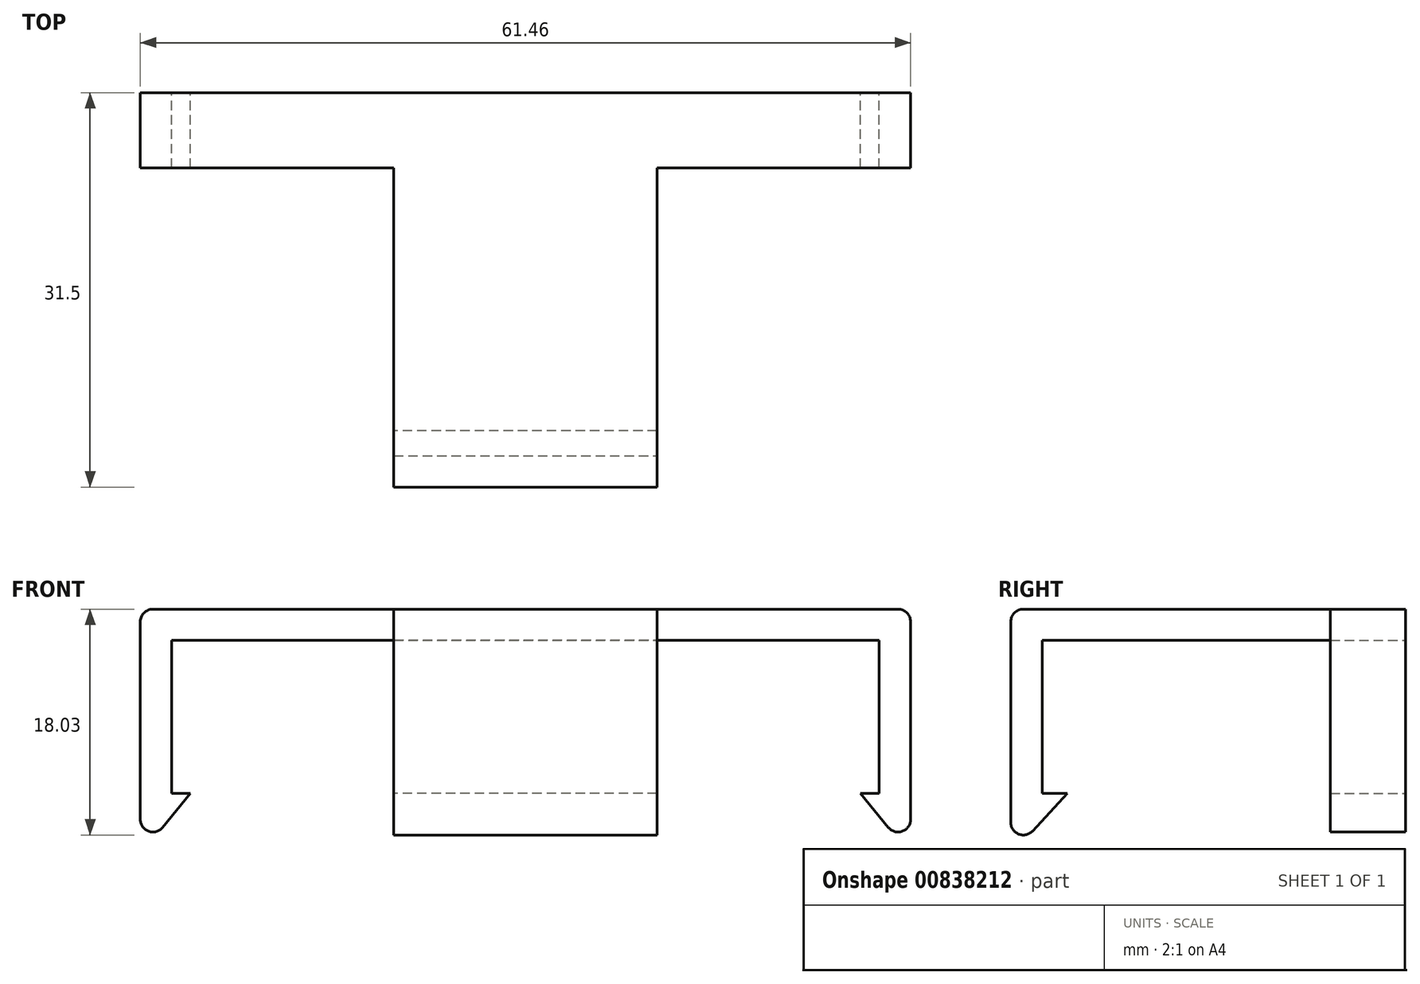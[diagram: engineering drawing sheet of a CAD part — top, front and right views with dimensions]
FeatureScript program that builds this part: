
annotation { "Feature Type Name" : "Feature", "Feature Type Description" : "" }
export const myFeature = defineFeature(function(context is Context, id is Id, definition is map)
    precondition{}
    {
        {
            var Q0;
            Q0=qCreatedBy(makeId("Front.planeOp"),FACE);
            var sketch = newSketch(context, id + "F0", { "sketchPlane" : qUnion([Q0])});
            skLineSegment(sketch, "E0.top", {"start": v(0, -12.2) * mm, "end": v(-1.5, -12.2) * mm});
            skLineSegment(sketch, "E0.left", {"start": v(0, 0) * mm, "end": v(0, -12.2) * mm, "construction": true});
            skLineSegment(sketch, "E1", {"start": v(2.5, -17.1) * mm, "end": v(2.5, 0) * mm});
            skLineSegment(sketch, "E2", {"start": v(0, 2.5) * mm, "end": v(-16.5, 2.5) * mm});
            skLineSegment(sketch, "E3", {"start": v(0, 0) * mm, "end": v(0, -12.2) * mm});
            skLineSegment(sketch, "E4", {"start": v(-10.1, 0) * mm, "end": v(0, 0) * mm});
            skLineSegment(sketch, "E5", {"start": v(0, 0) * mm, "end": v(0, 8.68) * mm, "construction": true});
            skLineSegment(sketch, "E6", {"start": v(0, -12.2) * mm, "end": v(0, -26.61) * mm, "construction": true});
            skPoint(sketch, "E7.orphan", {"position": v(-16.5, -14.7) * mm});
            skLineSegment(sketch, "E8", {"start": v(-1.5, -12.2) * mm, "end": v(2.5, -17.1) * mm});
            skLineSegment(sketch, "E9", {"start": v(2.5, 0) * mm, "end": v(2.5, 2.5) * mm});
            skLineSegment(sketch, "E10", {"start": v(2.5, 2.5) * mm, "end": v(0, 2.5) * mm});
            skLineSegment(sketch, "E11", {"start": v(-28.23, 8.15) * mm, "end": v(-28.23, -17.56) * mm, "construction": true});
            skLineSegment(sketch, "E12", {"start": v(-16.5, 2.5) * mm, "end": v(-28.23, 2.5) * mm});
            skLineSegment(sketch, "E13", {"start": v(-10.1, 0) * mm, "end": v(-28.23, 0) * mm});
            skLineSegment(sketch, "E14.MirrorCS", {"start": v(-39.96, 2.5) * mm, "end": v(-28.23, 2.5) * mm});
            skLineSegment(sketch, "E15.MirrorCS", {"start": v(-56.46, 2.5) * mm, "end": v(-39.96, 2.5) * mm});
            skLineSegment(sketch, "E16.MirrorCS", {"start": v(-46.36, 0) * mm, "end": v(-28.23, 0) * mm});
            skLineSegment(sketch, "E17.MirrorCS", {"start": v(-46.36, 0) * mm, "end": v(-56.46, 0) * mm});
            skLineSegment(sketch, "E18.MirrorCS", {"start": v(-58.96, 2.5) * mm, "end": v(-56.46, 2.5) * mm});
            skLineSegment(sketch, "E19.MirrorCS", {"start": v(-58.96, 0) * mm, "end": v(-58.96, 2.5) * mm});
            skLineSegment(sketch, "E20.MirrorCS", {"start": v(-58.96, -17.1) * mm, "end": v(-58.96, 0) * mm});
            skLineSegment(sketch, "E21.MirrorCS", {"start": v(-54.96, -12.2) * mm, "end": v(-58.96, -17.1) * mm});
            skLineSegment(sketch, "E22.MirrorCS", {"start": v(-56.46, -12.2) * mm, "end": v(-54.96, -12.2) * mm});
            skLineSegment(sketch, "E23.MirrorCS", {"start": v(-56.46, 0) * mm, "end": v(-56.46, -12.2) * mm, "construction": true});
            skLineSegment(sketch, "E24", {"start": v(-56.46, -12.2) * mm, "end": v(-56.46, 0) * mm});
            skSolve(sketch);
        }
        {
            var Q0;
            Q0=qSketchRegion(id+"F0",true);
            extrude(context, id + "F1", {"entities" : qUnion([Q0]), "depth" : 6 * mm, "offsetDistance" : 25 * mm});
        }
        {
            var Q0;
            Q0=makeQuery(id+"F1.opExtrude","SWEPT_EDGE",EDGE,{"disambiguationData":[OSD([sQuery(id+"F0.wireOp",EDGE,"E20.MirrorCS"),sQuery(id+"F0.wireOp",EDGE,"E21.MirrorCS")])]});
            var Q1;
            Q1=makeQuery(id+"F1.opExtrude","SWEPT_EDGE",EDGE,{"disambiguationData":[OSD([sQuery(id+"F0.wireOp",EDGE,"E1"),sQuery(id+"F0.wireOp",EDGE,"E8")])]});
            var Q2;
            Q2=makeQuery(id+"F1.opExtrude","SWEPT_EDGE",EDGE,{"disambiguationData":[OSD([sQuery(id+"F0.wireOp",EDGE,"E18.MirrorCS"),sQuery(id+"F0.wireOp",EDGE,"E19.MirrorCS")])]});
            var Q3;
            Q3=makeQuery(id+"F1.opExtrude","SWEPT_EDGE",EDGE,{"disambiguationData":[OSD([sQuery(id+"F0.wireOp",EDGE,"E9"),sQuery(id+"F0.wireOp",EDGE,"E10")])]});
            fillet(context, id + "F2", {"entities" : qUnion([Q0, Q1, Q2, Q3]), "radius" : 1 * mm, "tangentPropagation" : true, "allowEdgeOverflow" : false});
        }
        {
            var Q0;
            Q0=makeQuery(id+"F1.opExtrude","SWEPT_FACE",FACE,{"disambiguationData":[OSD([sQuery(id+"F0.wireOp",EDGE,"E2"),sQuery(id+"F0.wireOp",EDGE,"E10"),sQuery(id+"F0.wireOp",EDGE,"E12"),sQuery(id+"F0.wireOp",EDGE,"E14.MirrorCS"),sQuery(id+"F0.wireOp",EDGE,"E15.MirrorCS"),sQuery(id+"F0.wireOp",EDGE,"E18.MirrorCS")])]});
            var sketch = newSketch(context, id + "F3", { "sketchPlane" : qUnion([Q0])});
            skLineSegment(sketch, "E25", {"start": v(-28.23, 20.93) * mm, "end": v(-28.23, -70.2) * mm, "construction": true});
            skPoint(sketch, "E25.startSnap0", {"position": v(-28.23, 0) * mm});
            skLineSegment(sketch, "E26", {"start": v(-38.73, -6) * mm, "end": v(-38.73, -29) * mm});
            skLineSegment(sketch, "E27", {"start": v(-38.73, -29) * mm, "end": v(-28.23, -29) * mm});
            skLineSegment(sketch, "E28.MirrorCS", {"start": v(-17.73, -6) * mm, "end": v(-17.73, -29) * mm});
            skLineSegment(sketch, "E29.MirrorCS", {"start": v(-17.73, -29) * mm, "end": v(-28.23, -29) * mm});
            skSolve(sketch);
        }
        {
            var Q0;
            {var subQ1=sQuery(id+"F3.wireOp",EDGE,"E26");Q0=makeQuery(id+"F3.imprint","IMPRINT",FACE,{"disambiguationData":[TD([[makeQuery(id+"F3.imprint","IMPRINT",EDGE,{"derivedFrom":subQ1}),1.0]])]});}
            extrude(context, id + "F4", {"entities" : qUnion([Q0]), "operationType" : NewBodyOperationType.ADD, "oppositeDirection" : true, "depth" : 2.5 * mm, "offsetDistance" : 25 * mm});
        }
        {
            var Q0;
            Q0=makeQuery(id+"F4.opExtrude","SWEPT_FACE",FACE,{"disambiguationData":[OSD([sQuery(id+"F3.wireOp",EDGE,"E26")])]});
            var sketch = newSketch(context, id + "F5", { "sketchPlane" : qUnion([Q0])});
            skLineSegment(sketch, "E30", {"start": v(29, 2.5) * mm, "end": v(29, -12.2) * mm});
            skLineSegment(sketch, "E31", {"start": v(29, -12.2) * mm, "end": v(27, -12.2) * mm});
            skLineSegment(sketch, "E32", {"start": v(27, -12.2) * mm, "end": v(31.5, -17.1) * mm});
            skLineSegment(sketch, "E33", {"start": v(31.5, -17.1) * mm, "end": v(31.5, 2.5) * mm});
            skLineSegment(sketch, "E34", {"start": v(31.5, 2.5) * mm, "end": v(29, 2.5) * mm});
            skSolve(sketch);
        }
        {
            var Q0;
            Q0 = qSketchRegion(id + "F5", true);
            extrude(context, id + "F6", {"entities" : qUnion([Q0]), "operationType" : NewBodyOperationType.ADD, "oppositeDirection" : true, "depth" : 21 * mm, "offsetDistance" : 25 * mm});
        }
        {
            var Q0;
            Q0=makeQuery(id+"F6.opExtrude","SWEPT_EDGE",EDGE,{"disambiguationData":[OSD([sQuery(id+"F5.wireOp",EDGE,"E32"),sQuery(id+"F5.wireOp",EDGE,"E33")])]});
            fillet(context, id + "F7", {"entities" : qUnion([Q0]), "radius" : 1 * mm, "tangentPropagation" : true, "allowEdgeOverflow" : false});
        }
        {
            var Q0;
            Q0=makeQuery(id+"F6.opExtrude","SWEPT_EDGE",EDGE,{"disambiguationData":[OSD([sQuery(id+"F5.wireOp",EDGE,"E33"),sQuery(id+"F5.wireOp",EDGE,"E34")])]});
            fillet(context, id + "F8", {"entities" : qUnion([Q0]), "radius" : 1 * mm, "tangentPropagation" : true, "allowEdgeOverflow" : false});
        }
    });
